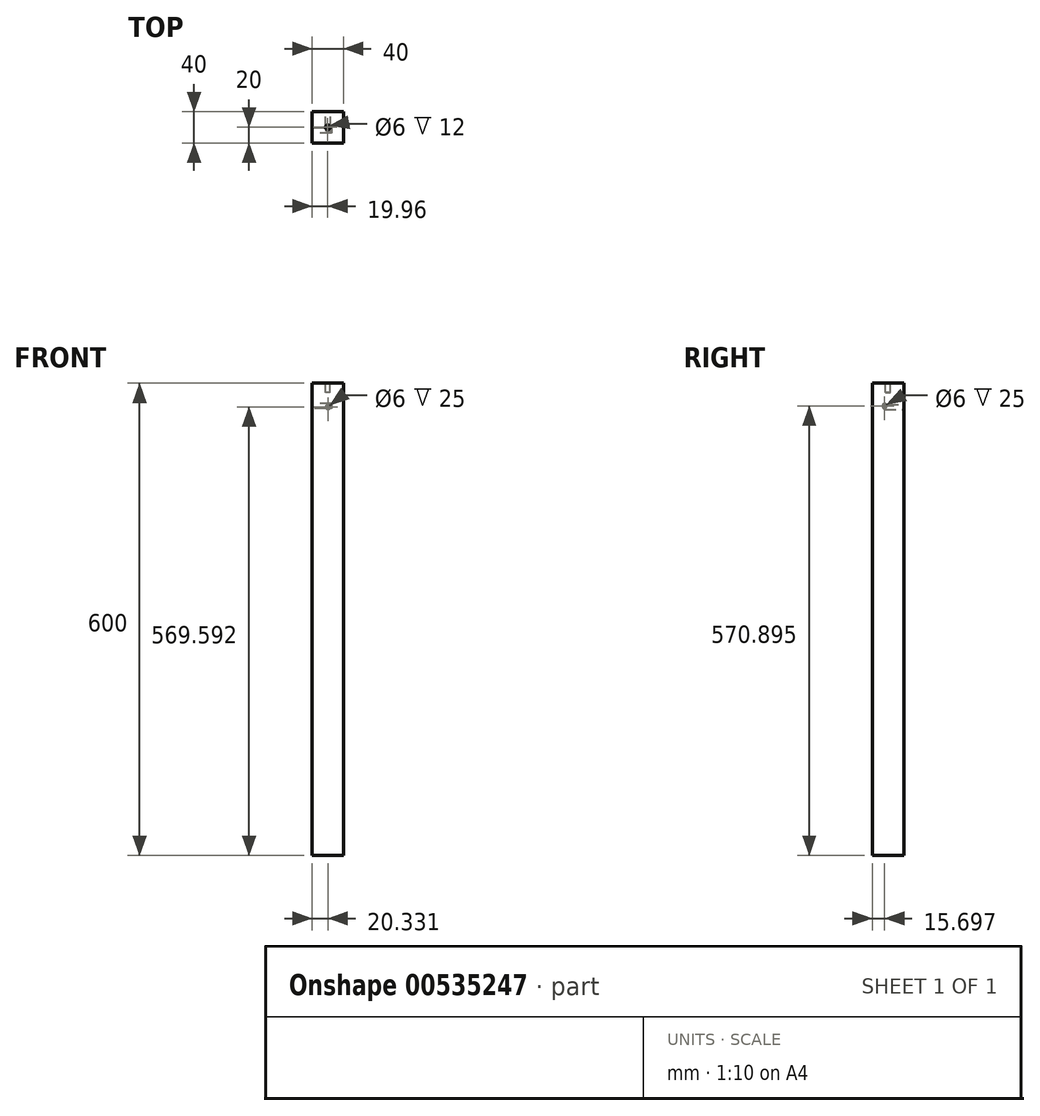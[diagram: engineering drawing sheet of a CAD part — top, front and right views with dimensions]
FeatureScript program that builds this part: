
annotation { "Feature Type Name" : "Feature", "Feature Type Description" : "" }
export const myFeature = defineFeature(function(context is Context, id is Id, definition is map)
    precondition{}
    {
        {
            var Q0;
            Q0=qCreatedBy(makeId("Top.planeOp"),FACE);
            var sketch = newSketch(context, id + "F0", { "sketchPlane" : qUnion([Q0])});
            skLineSegment(sketch, "E0.bottom", {"start": v(0, 0) * mm, "end": v(40, 0) * mm});
            skLineSegment(sketch, "E0.top", {"start": v(0, 40) * mm, "end": v(40, 40) * mm});
            skLineSegment(sketch, "E0.left", {"start": v(0, 0) * mm, "end": v(0, 40) * mm});
            skLineSegment(sketch, "E0.right", {"start": v(40, 0) * mm, "end": v(40, 40) * mm});
            skSolve(sketch);
        }
        {
            var Q0;
            Q0=qSketchRegion(id+"F0",true);
            extrude(context, id + "F1", {"entities" : qUnion([Q0]), "depth" : 600 * mm, "offsetDistance" : 25 * mm});
        }
        {
            var Q0;
            Q0=makeQuery(id+"F1.opExtrude","CAP_FACE",FACE,{"disambiguationData":[OSD([sQuery(id+"F0.wireOp",EDGE,"E0.bottom"),sQuery(id+"F0.wireOp",EDGE,"E0.top"),sQuery(id+"F0.wireOp",EDGE,"E0.left"),sQuery(id+"F0.wireOp",EDGE,"E0.right")])],"isStart":false});
            var sketch = newSketch(context, id + "F2", { "sketchPlane" : qUnion([Q0])});
            skCircle(sketch, "E1", {"center": v(19.96, 20) * mm, "radius": 3 * mm});
            skSolve(sketch);
        }
        {
            var Q0;
            Q0=makeQuery(id+"F2.imprint","IMPRINT",FACE,{"disambiguationData":[TD([[makeQuery(id+"F2.imprint","IMPRINT",EDGE,{"derivedFrom":sQuery(id+"F2.wireOp",EDGE,"E1")}),1.0]])]});
            extrude(context, id + "F3", {"entities" : qUnion([Q0]), "operationType" : NewBodyOperationType.REMOVE, "oppositeDirection" : true, "depth" : 12 * mm, "offsetDistance" : 25 * mm});
        }
        {
            var Q0;
            Q0=makeQuery(id+"F1.opExtrude","SWEPT_FACE",FACE,{"disambiguationData":[OSD([sQuery(id+"F0.wireOp",EDGE,"E0.left")])]});
            var sketch = newSketch(context, id + "F4", { "sketchPlane" : qUnion([Q0])});
            skCircle(sketch, "E2", {"center": v(-15.7, 570.9) * mm, "radius": 3 * mm});
            skSolve(sketch);
        }
        {
            var Q0;
            Q0=makeQuery(id+"F4.imprint","IMPRINT",FACE,{"disambiguationData":[TD([[makeQuery(id+"F4.imprint","IMPRINT",EDGE,{"derivedFrom":sQuery(id+"F4.wireOp",EDGE,"E2")}),1.0]])]});
            extrude(context, id + "F5", {"entities" : qUnion([Q0]), "operationType" : NewBodyOperationType.REMOVE, "oppositeDirection" : true, "depth" : 25 * mm, "offsetDistance" : 25 * mm});
        }
        {
            var Q0;
            Q0=makeQuery(id+"F1.opExtrude","SWEPT_FACE",FACE,{"disambiguationData":[OSD([sQuery(id+"F0.wireOp",EDGE,"E0.top")])]});
            var sketch = newSketch(context, id + "F6", { "sketchPlane" : qUnion([Q0])});
            skCircle(sketch, "E3", {"center": v(-20.33, 569.6) * mm, "radius": 3 * mm});
            skSolve(sketch);
        }
        {
            var Q0;
            Q0=makeQuery(id+"F6.imprint","IMPRINT",FACE,{"disambiguationData":[TD([[makeQuery(id+"F6.imprint","IMPRINT",EDGE,{"derivedFrom":sQuery(id+"F6.wireOp",EDGE,"E3")}),1.0]])]});
            extrude(context, id + "F7", {"entities" : qUnion([Q0]), "operationType" : NewBodyOperationType.REMOVE, "oppositeDirection" : true, "depth" : 25 * mm, "offsetDistance" : 25 * mm});
        }
    });
